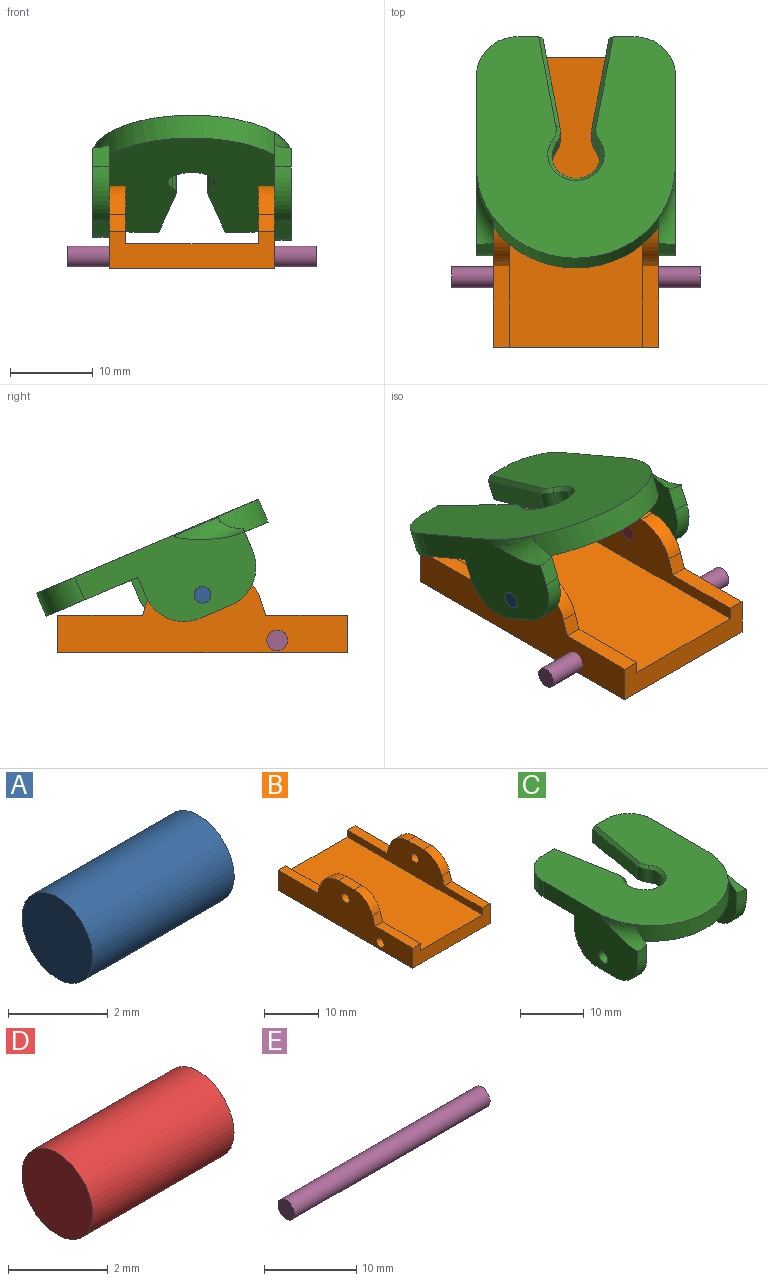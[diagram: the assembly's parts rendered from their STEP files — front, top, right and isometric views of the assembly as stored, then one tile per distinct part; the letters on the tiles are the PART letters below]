
ASSEMBLY  parts=5 mates=4
PART A: 3 faces, bbox 4x2x2 mm
  f0: cylinder r=1mm len=4mm, axis (-1,0,0), area 25.1mm2, adj f1,f2
  f1: plane 2x2mm, normal (1,0,0), area 3.1mm2, adj f0
  f2: plane 2x2mm, normal (-1,0,0), area 3.1mm2, adj f0
PART B: 25 faces, bbox 20x35x10 mm
  f0: plane 35x10mm, normal (1,0,0), area 218.7mm2, adj f2,f3,f5,f9,f10,f11,f13,f14
  f1: plane 4.06x2mm, normal (0,0,1), area 8.1mm2, adj f4,f6,f23,f24
  f2: plane 4.06x2mm, normal (0,0,1), area 8.1mm2, adj f0,f7,f21,f22
  f3: plane 20x4.51mm, normal (0,1,0), area 66.1mm2, adj f0,f4,f6,f7,f8,f9,f15,f20
  f4: plane 35x10mm, normal (-1,0,0), area 218.7mm2, adj f1,f3,f5,f9,f10,f12,f17,f18
  f5: plane 20x4.51mm, normal (0,-1,0), area 66.1mm2, adj f0,f4,f6,f7,f8,f9,f14,f17
  f6: plane 35x7mm, normal (1,0,0), area 116.8mm2, adj f1,f3,f5,f8,f12,f17,f18,f19
  f7: plane 35x7mm, normal (-1,0,0), area 116.8mm2, adj f2,f3,f5,f8,f11,f13,f14,f15
  f8: plane 35x16mm, normal (0,0,1), area 560mm2, adj f3,f5,f6,f7
  f9: plane 35x20mm, normal (0,0,-1), area 700mm2, adj f0,f3,f4,f5
  f10: cylinder r=1mm len=20mm, axis (1,0,0), area 125.7mm2, adj f0,f4
  f11: cylinder r=1mm len=2mm, axis (1,0,0), area 12.6mm2, adj f0,f7
  f12: cylinder r=1mm len=2mm, axis (1,0,0), area 12.6mm2, adj f4,f6
  f13: plane 2.03x2mm, normal (0,-0.95,0.31), area 4.3mm2, adj f0,f7,f14,f22
  f14: plane 9.86x2mm, normal (0,0,1), area 19.7mm2, adj f0,f5,f7,f13
  f15: plane 10.26x2mm, normal (0,0,1), area 20.5mm2, adj f0,f3,f7,f16
  f16: plane 2.03x2mm, normal (0,0.95,0.31), area 4.3mm2, adj f0,f7,f15,f21
  f17: plane 9.86x2mm, normal (0,0,1), area 19.7mm2, adj f4,f5,f6,f18
  f18: plane 2.03x2mm, normal (0,-0.95,0.31), area 4.3mm2, adj f4,f6,f17,f23
  f19: plane 2.03x2mm, normal (0,0.95,0.31), area 4.3mm2, adj f4,f6,f20,f24
  f20: plane 10.26x2mm, normal (0,0,1), area 20.5mm2, adj f3,f4,f6,f19
  f21: cylinder r=5mm len=4.76mm, axis (-1,0,0), area 12.6mm2, adj f0,f2,f7,f16
  f22: cylinder r=5mm len=4.76mm, axis (1,0,0), area 12.6mm2, adj f0,f2,f7,f13
  f23: cylinder r=5mm len=4.76mm, axis (1,0,0), area 12.6mm2, adj f1,f4,f6,f18
  f24: cylinder r=5mm len=4.76mm, axis (-1,0,0), area 12.6mm2, adj f1,f4,f6,f19
PART C: 37 faces, bbox 36.7x29.4x12.5 mm
  f0: plane 29.1x24mm, normal (0,0,-1), area 485.5mm2, adj f3,f4,f8,f10,f11,f12,f13,f14
  f1: plane 2.96x2.04mm, normal (0,-1,0), area 5.3mm2, adj f3,f4,f6,f9,f28
  f2: plane 4.02x2mm, normal (0,0,-1), area 8mm2, adj f3,f4,f6,f7
  f3: plane 21.01x10.49mm, normal (-1,0,0), area 137.7mm2, adj f0,f1,f2,f5,f6,f7,f8,f9
  f4: plane 14.02x10.39mm, normal (1,0,0), area 93.7mm2, adj f0,f1,f2,f5,f6,f7,f8,f10
  f5: cylinder r=1mm len=2mm, axis (1,0,0), area 12.6mm2, adj f3,f4
  f6: cylinder r=5mm len=5mm, axis (-1,0,0), area 15.7mm2, adj f1,f2,f3,f4
  f7: cylinder r=5mm len=5.49mm, axis (-1,0,0), area 16.7mm2, adj f2,f3,f4,f8
  f8: plane 2x2mm, normal (0,1,0), area 4mm2, adj f0,f3,f4,f7
  f9: plane 0.04x0.03mm, normal (0,0,1), area 0mm2, adj f1,f3,f28
  f10: cylinder r=12.02mm len=24mm, axis (0,0,-1), area 72.2mm2, adj f0,f3,f4,f11,f17,f21,f25,f28
  f11: plane 21.01x10.49mm, normal (1,0,0), area 143.5mm2, adj f0,f10,f17,f18,f19,f20,f22,f23
  f12: plane 3x3mm, normal (0,1,0), area 8.9mm2, adj f0,f13,f17,f30,f32
  f13: plane 11.71x2.5mm, normal (-0.98,0.17,0), area 29.7mm2, adj f0,f12,f26,f32
  f14: cylinder r=2.9mm len=5.81mm, axis (0,0,-1), area 31.5mm2, adj f0,f26,f27,f34
  f15: plane 11.71x2.5mm, normal (0.98,0.17,0), area 29.7mm2, adj f0,f16,f27,f36
  f16: plane 3x3mm, normal (0,1,0), area 8.9mm2, adj f0,f15,f17,f31,f36
  f17: plane 29.1x24mm, normal (0,0,1), area 504.9mm2, adj f3,f10,f11,f12,f16,f30,f31,f32
  f18: plane 2.94x2.04mm, normal (0,-1,0), area 5.2mm2, adj f11,f21,f22,f24,f25
  f19: plane 4.89x2mm, normal (0,0,-1), area 9.8mm2, adj f11,f21,f22,f23
  f20: plane 2.49x2mm, normal (0,1,0), area 5mm2, adj f0,f11,f21,f23
  f21: plane 14.89x10.39mm, normal (-1,0,0), area 100.3mm2, adj f0,f10,f18,f19,f20,f22,f23,f25
  f22: cylinder r=5mm len=5mm, axis (1,0,0), area 15.7mm2, adj f11,f18,f19,f21
  f23: cylinder r=5mm len=5mm, axis (1,0,0), area 15.7mm2, adj f11,f19,f20,f21
  f24: plane 0.09x0.07mm, normal (0,0,1), area 0mm2, adj f11,f18,f25
  f25: torus R=14.92mm, axis (0,0,1), area 17.6mm2, adj f10,f11,f18,f21,f24
  f26: cylinder r=2.9mm len=2.5mm, axis (0,0,-1), area 5.6mm2, adj f0,f13,f14,f33
  f27: cylinder r=2.9mm len=2.5mm, axis (0,0,-1), area 5.6mm2, adj f0,f14,f15,f35
  f28: torus R=14.92mm, axis (0,0,-1), area 17mm2, adj f1,f3,f4,f9,f10
  f29: cylinder r=1mm len=2mm, axis (-1,0,0), area 12.6mm2, adj f11,f21
  f30: cylinder r=5mm len=5mm, axis (0,0,-1), area 23.6mm2, adj f0,f11,f12,f17
  f31: cylinder r=5mm len=5mm, axis (0,0,-1), area 23.6mm2, adj f0,f3,f16,f17
  f32: plane 11.8x2.57mm, normal (-0.7,0.12,0.71), area 8.4mm2, adj f12,f13,f17,f33
  f33: cone r=2.4mm half-angle=45deg, axis (0,0,-1), area 1.5mm2, adj f17,f26,f32,f34
  f34: cone r=2.9mm half-angle=45deg, axis (0,0,1), area 9.7mm2, adj f14,f17,f33,f35
  f35: cone r=2.4mm half-angle=45deg, axis (0,0,-1), area 1.5mm2, adj f17,f27,f34,f36
  f36: plane 11.8x2.57mm, normal (0.7,0.12,0.71), area 8.4mm2, adj f15,f16,f17,f35
PART D: 3 faces, bbox 4x2x2 mm
  f0: cylinder r=1mm len=4mm, axis (-1,0,0), area 25.1mm2, adj f1,f2
  f1: plane 2x2mm, normal (1,0,0), area 3.1mm2, adj f0
  f2: plane 2x2mm, normal (-1,0,0), area 3.1mm2, adj f0
PART E: 3 faces, bbox 30x2.5x2.5 mm
  f0: plane 2.5x2.5mm, normal (-1,0,0), area 4.9mm2, adj f1
  f1: cylinder r=1.25mm len=30mm, axis (1,0,0), area 235.6mm2, adj f0,f2
  f2: plane 2.5x2.5mm, normal (1,0,0), area 4.9mm2, adj f1
PLACE A rot(axis=(-1,0,0),23deg) t=(-73.38,50.74,-42.4)mm
PLACE B t=(-53.38,67.87,-6.22)mm fixed
PLACE C rot(axis=(-1,0,0),23deg) t=(-53.38,50.74,-42.4)mm
PLACE D rot(axis=(-1,0,0),23deg) t=(-33.38,50.74,-42.4)mm
PLACE E t=(-53.38,96.87,-6.22)mm
MATE fastened B.f10 <-> E.f1  axis (-1,0,0) through (-78.38,-38.63,12.28)mm
MATE revolute A.f0 <-> B.f11  axis (1,0,0) through (-76.38,-29.61,17.78)mm
MATE fastened A.f0 <-> C.f5  axis (-1,0,0) through (-80.38,-29.61,17.78)mm
MATE fastened D.f0 <-> C.f5  axis (1,0,0) through (-56.38,-29.61,17.78)mm
